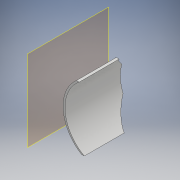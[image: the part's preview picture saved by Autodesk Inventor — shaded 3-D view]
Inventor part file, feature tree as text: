
AUTODESK INVENTOR PART (.ipt)
format: ipt  version: 2018 (Build 220112000, 112)  size: 1,113,088 bytes
history: native  units: mm
features: extrude x4, sketch x4, plane x1
ambient origin geometry x8: Origin, YZ Plane, XZ Plane, XY Plane, X Axis, Y Axis, Z Axis, Center Point
bodies: Solid1 (feature_tree)
feature tree (9):
  extrude  "Extrusion1"  Depth=12.0mm TaperAngle=0.0deg
  plane  "Work Plane1"
  sketch  "Sketch2"  dims[d8=-10.0mm d9=10.0mm]
  extrude  "Extrusion2"  Depth=10.0mm
  extrude  "Extrusion3"  Depth=4.0mm
  extrude  "Extrusion4"  Depth=10.0mm
  sketch  "Sketch1"  dims[d0=12.0mm d1=12.0mm d2=0.0mm]
  sketch  "Sketch3"  dims[d10=6.5mm d12=4.0mm]
  sketch  "Sketch4"  dims[d14=3.0mm d15=3.0mm d16=10.0mm d17=0.0mm d18=10.0mm d19=0.0mm d20=0.45mm d21=0.45mm d22=10.0mm d23=0.0mm]
